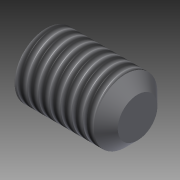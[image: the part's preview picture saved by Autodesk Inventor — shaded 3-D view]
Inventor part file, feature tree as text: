
AUTODESK INVENTOR PART (.ipt)
format: ipt  version: 2014 SP2 (Build 180246200, 246)  size: 135,680 bytes
history: native  units: mm
features: other x14, sketch x2, revolve x1, thread x1, extrude x1
ambient origin geometry x8: Origin, YZ Plane, XZ Plane, XY Plane, X Axis, Y Axis, Z Axis, Center Point
bodies: Solid1 (feature_tree)
feature tree (19):
  revolve  "Revolution1"  [1 undecoded]
  thread  "Thread1"  [1 undecoded]
  extrude  "Extrusion1"  [1 undecoded]
  other  "IP1_XY"
  other  "IP1_YZ"
  other  "IP1_ZX"
  other  "IP1_X"
  other  "IP1_Y"
  other  "IP1_Z"
  other  "IP1_Center"
  other  "IP2_XY"
  other  "IP2_YZ"
  other  "IP2_ZX"
  other  "IP2_X"
  other  "IP2_Y"
  other  "IP2_Z"
  other  "IP2_Center"
  sketch  "Sketch_1"  dims[d0=360.0deg d1=5.00203mm d2=0.0mm d3=2.5mm d4=0.0mm]
  sketch  "Sketch_2"  dims[d5=0.0mm d6=0.0mm]
note: 3 required parameter values undecoded (feature->parameter linkage not recoverable at this tier; creation-order binding heuristic only, values carry confidence <= 0.55)